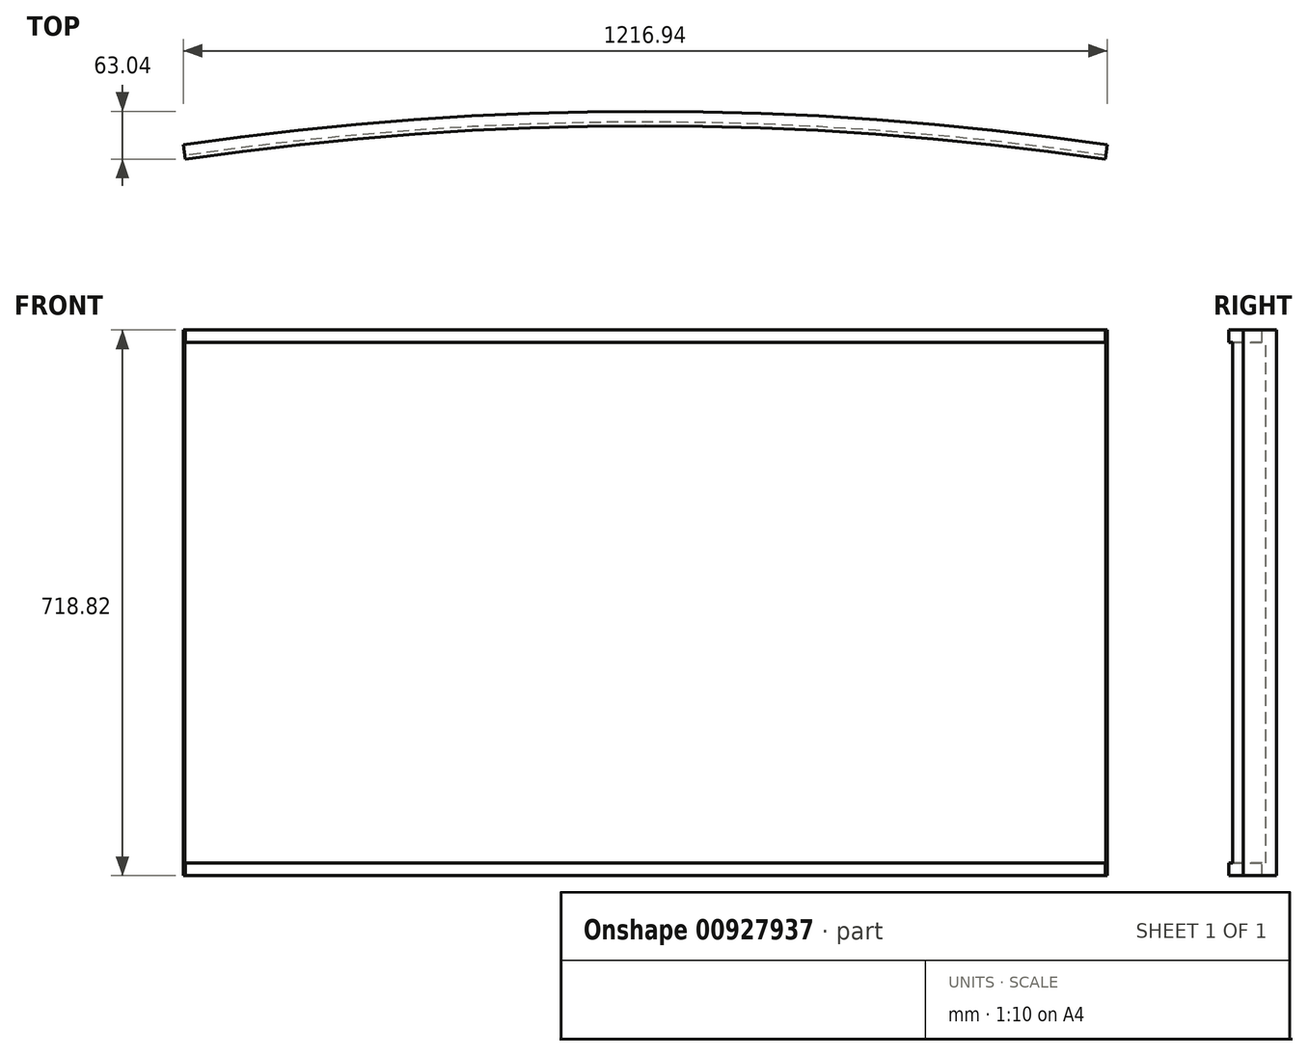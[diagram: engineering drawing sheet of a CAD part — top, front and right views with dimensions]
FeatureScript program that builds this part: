
annotation { "Feature Type Name" : "Feature", "Feature Type Description" : "" }
export const myFeature = defineFeature(function(context is Context, id is Id, definition is map)
    precondition{}
    {
        {
            var Q0;
            Q0=qCreatedBy(makeId("Right.planeOp"),FACE);
            var sketch = newSketch(context, id + "F0", { "sketchPlane" : qUnion([Q0])});
            skLineSegment(sketch, "E0", {"start": v(0, 332.9) * mm, "end": v(0, 0) * mm});
            skLineSegment(sketch, "E1", {"start": v(0, 0) * mm, "end": v(0, -352.9) * mm});
            skLineSegment(sketch, "E2", {"start": v(0, 332.9) * mm, "end": v(-5.08, 332.9) * mm});
            skLineSegment(sketch, "E3", {"start": v(-5.08, 332.9) * mm, "end": v(-5.08, 349.41) * mm});
            skLineSegment(sketch, "E4", {"start": v(-5.08, 349.41) * mm, "end": v(13.97, 349.41) * mm});
            skLineSegment(sketch, "E5", {"start": v(13.97, 349.41) * mm, "end": v(13.97, -369.4) * mm});
            skLineSegment(sketch, "E6", {"start": v(13.97, -369.4) * mm, "end": v(-5.08, -369.4) * mm});
            skLineSegment(sketch, "E7", {"start": v(-5.08, -369.4) * mm, "end": v(-5.08, -352.9) * mm});
            skLineSegment(sketch, "E8", {"start": v(-5.08, -352.9) * mm, "end": v(0, -352.9) * mm});
            skSolve(sketch);
        }
        {
            var Q0;
            Q0=qCreatedBy(makeId("Right.planeOp"),FACE);
            var sketch = newSketch(context, id + "F1", { "sketchPlane" : qUnion([Q0])});
            skLineSegment(sketch, "E9", {"start": v(-4197.1, 2031.4) * mm, "end": v(-4197.1, 0) * mm, "construction": true});
            skLineSegment(sketch, "E10", {"start": v(-4197.1, 0) * mm, "end": v(-4197.1, -2052.99) * mm, "construction": true});
            skSolve(sketch);
        }
        {
            var Q0;
            Q0=makeQuery(id+"F0.imprint","IMPRINT",FACE,{"disambiguationData":[TD([[makeQuery(id+"F0.imprint","IMPRINT",EDGE,{"derivedFrom":sQuery(id+"F0.wireOp",EDGE,"E0")}),1.0]])]});
            var Q1;
            Q1=sQuery(id+"F1.wireOp",EDGE,"E9");
            revolve(context, id + "F2", {"surfaceOperationType" : NewSurfaceOperationType.NEW, "entities" : qUnion([Q0]), "axis" : qUnion([Q1]), "revolveType" : RevolveType.SYMMETRIC, "angle" : 0.29 * radian});
        }
    });
